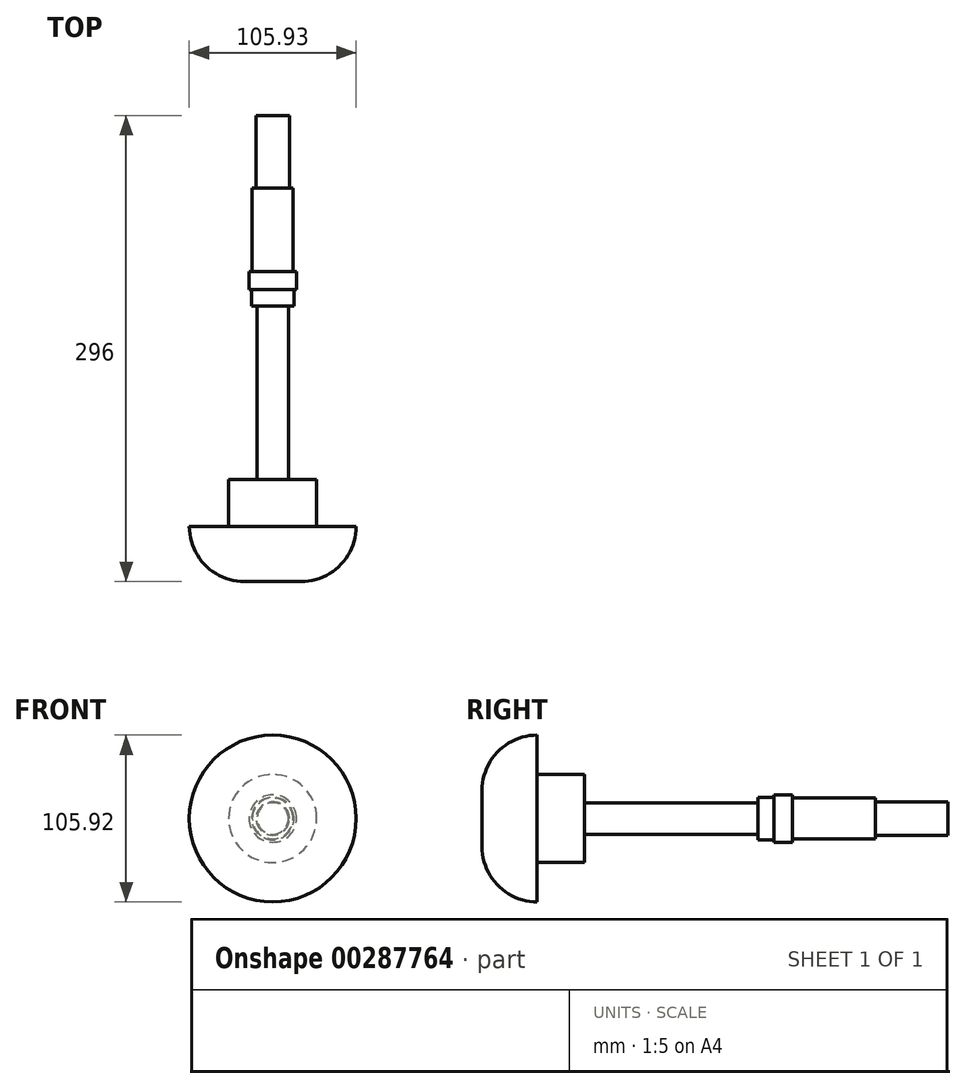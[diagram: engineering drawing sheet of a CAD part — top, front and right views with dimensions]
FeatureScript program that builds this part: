
annotation { "Feature Type Name" : "Feature", "Feature Type Description" : "" }
export const myFeature = defineFeature(function(context is Context, id is Id, definition is map)
    precondition{}
    {
        {
            var Q0;
            Q0=qCreatedBy(makeId("Front.planeOp"),FACE);
            var sketch = newSketch(context, id + "F0", { "sketchPlane" : qUnion([Q0])});
            skCircle(sketch, "E0", {"center": v(-0.03, 0.01) * mm, "radius": 27.96 * mm});
            skSolve(sketch);
        }
        {
            var Q0;
            Q0=makeQuery(id+"F0.imprint","IMPRINT",FACE,{"disambiguationData":[TD([[makeQuery(id+"F0.imprint","IMPRINT",EDGE,{"derivedFrom":sQuery(id+"F0.wireOp",EDGE,"E0")}),1.0]])]});
            extrude(context, id + "F1", {"entities" : qUnion([Q0]), "depth" : 30 * mm});
        }
        {
            var Q0;
            Q0=makeQuery(id+"F1.opExtrude","CAP_FACE",FACE,{"disambiguationData":[OSD([sQuery(id+"F0.wireOp",EDGE,"E0")])],"isStart":false});
            var sketch = newSketch(context, id + "F2", { "sketchPlane" : qUnion([Q0])});
            skCircle(sketch, "E1", {"center": v(-0.03, 0.01) * mm, "radius": 52.96 * mm});
            skSolve(sketch);
        }
        {
            var Q0;
            Q0=makeQuery(id+"F2.imprint","IMPRINT",FACE,{"disambiguationData":[TD([[makeQuery(id+"F2.imprint","IMPRINT",EDGE,{"derivedFrom":sQuery(id+"F2.wireOp",EDGE,"E1")}),1.0]])]});
            var Q1;
            Q1=makeQuery(id+"F2.imprint","IMPRINT",FACE,{"disambiguationData":[TD([[makeQuery(id+"F2.imprint","IMPRINT",EDGE,{"derivedFrom":makeQuery(id+"F1.opExtrude","CAP_EDGE",EDGE,{"disambiguationData":[OSD([sQuery(id+"F0.wireOp",EDGE,"E0")])],"isStart":false})}),1.0]])]});
            extrude(context, id + "F3", {"entities" : qUnion([Q0, Q1]), "operationType" : NewBodyOperationType.ADD, "depth" : 35 * mm});
        }
        {
            var Q0;
            Q0=makeQuery(id+"F3.opExtrude","CAP_EDGE",EDGE,{"disambiguationData":[OSD([sQuery(id+"F2.wireOp",EDGE,"E1")])],"isStart":false});
            fillet(context, id + "F4", {"entities" : qUnion([Q0]), "radius" : 35 * mm, "tangentPropagation" : true, "allowEdgeOverflow" : false});
        }
        {
            var Q0;
            Q0=makeQuery(id+"F1.opExtrude","CAP_FACE",FACE,{"disambiguationData":[OSD([sQuery(id+"F0.wireOp",EDGE,"E0")])],"isStart":true});
            var sketch = newSketch(context, id + "F5", { "sketchPlane" : qUnion([Q0])});
            skCircle(sketch, "E2", {"center": v(0.03, 0.01) * mm, "radius": 9.99 * mm});
            skSolve(sketch);
        }
        {
            var Q0;
            Q0=makeQuery(id+"F5.imprint","IMPRINT",FACE,{"disambiguationData":[TD([[makeQuery(id+"F5.imprint","IMPRINT",EDGE,{"derivedFrom":sQuery(id+"F5.wireOp",EDGE,"E2")}),1.0]])]});
            extrude(context, id + "F6", {"entities" : qUnion([Q0]), "operationType" : NewBodyOperationType.ADD, "depth" : 110.2 * mm});
        }
        {
            var Q0;
            Q0=makeQuery(id+"F6.opExtrude","CAP_FACE",FACE,{"disambiguationData":[OSD([sQuery(id+"F5.wireOp",EDGE,"E2")])],"isStart":false});
            var sketch = newSketch(context, id + "F7", { "sketchPlane" : qUnion([Q0])});
            skCircle(sketch, "E3", {"center": v(0.03, 0.01) * mm, "radius": 13.5 * mm});
            skSolve(sketch);
        }
        {
            var Q0;
            Q0=makeQuery(id+"F7.imprint","IMPRINT",FACE,{"disambiguationData":[TD([[makeQuery(id+"F7.imprint","IMPRINT",EDGE,{"derivedFrom":sQuery(id+"F7.wireOp",EDGE,"E3")}),1.0]])]});
            var Q1;
            Q1=makeQuery(id+"F7.imprint","IMPRINT",FACE,{"disambiguationData":[TD([[makeQuery(id+"F7.imprint","IMPRINT",EDGE,{"derivedFrom":makeQuery(id+"F6.opExtrude","CAP_EDGE",EDGE,{"disambiguationData":[OSD([sQuery(id+"F5.wireOp",EDGE,"E2")])],"isStart":false})}),1.0]])]});
            extrude(context, id + "F8", {"entities" : qUnion([Q0, Q1]), "operationType" : NewBodyOperationType.ADD, "depth" : 10.2 * mm});
        }
        {
            var Q0;
            Q0=makeQuery(id+"F8.opExtrude","CAP_FACE",FACE,{"disambiguationData":[OSD([sQuery(id+"F7.wireOp",EDGE,"E3")])],"isStart":false});
            var sketch = newSketch(context, id + "F9", { "sketchPlane" : qUnion([Q0])});
            skCircle(sketch, "E4", {"center": v(0.03, 0.01) * mm, "radius": 15.08 * mm});
            skSolve(sketch);
        }
        {
            var Q0;
            Q0=makeQuery(id+"F9.imprint","IMPRINT",FACE,{"disambiguationData":[TD([[makeQuery(id+"F9.imprint","IMPRINT",EDGE,{"derivedFrom":makeQuery(id+"F8.opExtrude","CAP_EDGE",EDGE,{"disambiguationData":[OSD([sQuery(id+"F7.wireOp",EDGE,"E3")])],"isStart":false})}),1.0]])]});
            var Q1;
            Q1=makeQuery(id+"F9.imprint","IMPRINT",FACE,{"disambiguationData":[TD([[makeQuery(id+"F9.imprint","IMPRINT",EDGE,{"derivedFrom":sQuery(id+"F9.wireOp",EDGE,"E4")}),1.0]])]});
            extrude(context, id + "F10", {"entities" : qUnion([Q0, Q1]), "operationType" : NewBodyOperationType.ADD, "depth" : 11.6 * mm});
        }
        {
            var Q0;
            Q0=makeQuery(id+"F10.opExtrude","CAP_FACE",FACE,{"disambiguationData":[OSD([sQuery(id+"F9.wireOp",EDGE,"E4")])],"isStart":false});
            var sketch = newSketch(context, id + "F11", { "sketchPlane" : qUnion([Q0])});
            skCircle(sketch, "E5", {"center": v(0.03, 0.01) * mm, "radius": 13 * mm});
            skSolve(sketch);
        }
        {
            var Q0;
            Q0=makeQuery(id+"F11.imprint","IMPRINT",FACE,{"disambiguationData":[TD([[makeQuery(id+"F11.imprint","IMPRINT",EDGE,{"derivedFrom":sQuery(id+"F11.wireOp",EDGE,"E5")}),1.0]])]});
            extrude(context, id + "F12", {"entities" : qUnion([Q0]), "operationType" : NewBodyOperationType.ADD, "depth" : 53 * mm});
        }
        {
            var Q0;
            Q0=makeQuery(id+"F12.opExtrude","CAP_FACE",FACE,{"disambiguationData":[OSD([sQuery(id+"F11.wireOp",EDGE,"E5")])],"isStart":false});
            var sketch = newSketch(context, id + "F13", { "sketchPlane" : qUnion([Q0])});
            skCircle(sketch, "E6", {"center": v(0.03, 0.01) * mm, "radius": 10.6 * mm});
            skSolve(sketch);
        }
        {
            var Q0;
            Q0=qSketchRegion(id+"F13",true);
            extrude(context, id + "F14", {"entities" : qUnion([Q0]), "operationType" : NewBodyOperationType.ADD, "depth" : 46 * mm});
        }
    });
